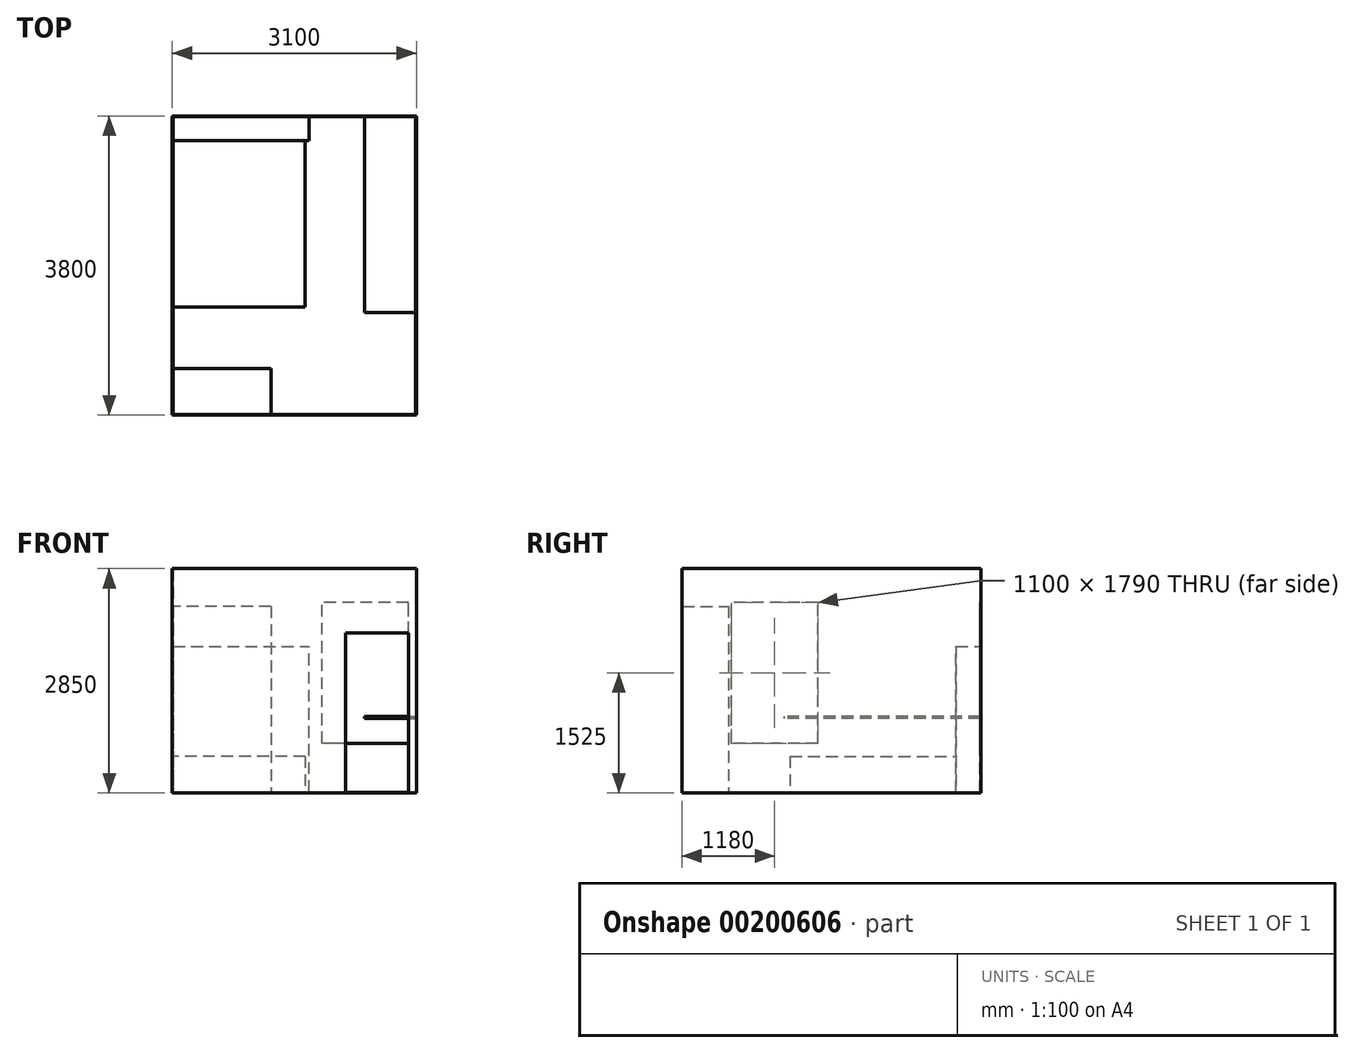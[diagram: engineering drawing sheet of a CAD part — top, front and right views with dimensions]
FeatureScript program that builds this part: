
annotation { "Feature Type Name" : "Feature", "Feature Type Description" : "" }
export const myFeature = defineFeature(function(context is Context, id is Id, definition is map)
    precondition{}
    {
        {
            var Q0;
            Q0=qCreatedBy(makeId("Top.planeOp"),FACE);
            var sketch = newSketch(context, id + "F0", { "sketchPlane" : qUnion([Q0])});
            skLineSegment(sketch, "E0.bottom", {"start": v(1550, -1900) * mm, "end": v(-1550, -1900) * mm});
            skLineSegment(sketch, "E0.top", {"start": v(1550, 1900) * mm, "end": v(-1550, 1900) * mm});
            skLineSegment(sketch, "E0.left", {"start": v(1550, -1900) * mm, "end": v(1550, 1900) * mm});
            skLineSegment(sketch, "E0.right", {"start": v(-1550, -1900) * mm, "end": v(-1550, 1900) * mm});
            skPoint(sketch, "E0.middle", {"position": v(0, 0) * mm});
            skSolve(sketch);
        }
        {
            var Q0;
            Q0 = qSketchRegion(id + "F0", true);
            extrude(context, id + "F1", {"entities" : qUnion([Q0]), "depth" : 2850 * mm});
        }
        {
            var Q0;
            Q0=makeQuery(id+"F1.opExtrude","CAP_FACE",FACE,{"disambiguationData":[OSD([sQuery(id+"F0.wireOp",EDGE,"E0.bottom"),sQuery(id+"F0.wireOp",EDGE,"E0.top"),sQuery(id+"F0.wireOp",EDGE,"E0.left"),sQuery(id+"F0.wireOp",EDGE,"E0.right")])],"isStart":false});
            shell(context, id + "F2", {"entities" : qUnion([Q0]), "thickness" : 10 * mm});
        }
        {
            var Q0;
            Q0=makeQuery(id+"F1.opExtrude","SWEPT_FACE",FACE,{"disambiguationData":[OSD([sQuery(id+"F0.wireOp",EDGE,"E0.bottom")])]});
            var sketch = newSketch(context, id + "F3", { "sketchPlane" : qUnion([Q0])});
            skLineSegment(sketch, "E1.bottom", {"start": v(650, 0) * mm, "end": v(1450, 0) * mm});
            skLineSegment(sketch, "E1.top", {"start": v(650, 2030) * mm, "end": v(1450, 2030) * mm});
            skLineSegment(sketch, "E1.left", {"start": v(650, 0) * mm, "end": v(650, 2030) * mm});
            skLineSegment(sketch, "E1.right", {"start": v(1450, 0) * mm, "end": v(1450, 2030) * mm});
            skSolve(sketch);
        }
        {
            var Q0;
            Q0 = qSketchRegion(id + "F3", true);
            extrude(context, id + "F4", {"entities" : qUnion([Q0]), "operationType" : NewBodyOperationType.REMOVE, "oppositeDirection" : true, "depth" : 10 * mm});
        }
        {
            var Q0;
            Q0=makeQuery(id+"F1.opExtrude","SWEPT_FACE",FACE,{"disambiguationData":[OSD([sQuery(id+"F0.wireOp",EDGE,"E0.right")])]});
            var sketch = newSketch(context, id + "F5", { "sketchPlane" : qUnion([Q0])});
            skLineSegment(sketch, "E2.bottom", {"start": v(170, 630) * mm, "end": v(1270, 630) * mm});
            skLineSegment(sketch, "E2.top", {"start": v(170, 2420) * mm, "end": v(1270, 2420) * mm});
            skLineSegment(sketch, "E2.left", {"start": v(170, 630) * mm, "end": v(170, 2420) * mm});
            skLineSegment(sketch, "E2.right", {"start": v(1270, 630) * mm, "end": v(1270, 2420) * mm});
            skSolve(sketch);
        }
        {
            var Q0;
            Q0 = qSketchRegion(id + "F5", true);
            extrude(context, id + "F6", {"entities" : qUnion([Q0]), "operationType" : NewBodyOperationType.REMOVE, "oppositeDirection" : true, "depth" : 10 * mm});
        }
        {
            var Q0;
            Q0=makeQuery(id+"F1.opExtrude","SWEPT_FACE",FACE,{"disambiguationData":[OSD([sQuery(id+"F0.wireOp",EDGE,"E0.top")])]});
            var sketch = newSketch(context, id + "F7", { "sketchPlane" : qUnion([Q0])});
            skLineSegment(sketch, "E3.bottom", {"start": v(-1450, 630) * mm, "end": v(-350, 630) * mm});
            skLineSegment(sketch, "E3.top", {"start": v(-1450, 2420) * mm, "end": v(-350, 2420) * mm});
            skLineSegment(sketch, "E3.left", {"start": v(-1450, 630) * mm, "end": v(-1450, 2420) * mm});
            skLineSegment(sketch, "E3.right", {"start": v(-350, 630) * mm, "end": v(-350, 2420) * mm});
            skSolve(sketch);
        }
        {
            var Q0;
            Q0 = qSketchRegion(id + "F7", true);
            extrude(context, id + "F8", {"entities" : qUnion([Q0]), "operationType" : NewBodyOperationType.REMOVE, "oppositeDirection" : true, "depth" : 10 * mm});
        }
        {
            var Q0;
            Q0=makeQuery(id+"F2.opShell","OFFSET_FACE",FACE,{"disambiguationData":[OSD([sQuery(id+"F0.wireOp",EDGE,"E0.bottom"),sQuery(id+"F0.wireOp",EDGE,"E0.top"),sQuery(id+"F0.wireOp",EDGE,"E0.left"),sQuery(id+"F0.wireOp",EDGE,"E0.right")])]});
            var sketch = newSketch(context, id + "F9", { "sketchPlane" : qUnion([Q0])});
            skLineSegment(sketch, "E4.bottom", {"start": v(-1540, -1890) * mm, "end": v(-295.4, -1890) * mm});
            skLineSegment(sketch, "E4.top", {"start": v(-1540, -1305.8) * mm, "end": v(-295.4, -1305.8) * mm});
            skLineSegment(sketch, "E4.left", {"start": v(-1540, -1890) * mm, "end": v(-1540, -1305.8) * mm});
            skLineSegment(sketch, "E4.right", {"start": v(-295.4, -1890) * mm, "end": v(-295.4, -1305.8) * mm});
            skSolve(sketch);
        }
        {
            var Q0;
            Q0 = qSketchRegion(id + "F9", true);
            var Q1;
            Q1 = qConstructionFilter(qBodyType(qCreatedBy(id + "F9" ,EDGE), BodyType.WIRE), ConstructionObject.NO);
            extrude(context, id + "F10", {"entities" : qUnion([Q0]), "operationType" : NewBodyOperationType.ADD, "surfaceEntities" : qUnion([Q1]), "depth" : 2362.2 * mm});
        }
        {
            var Q0;
            Q0=makeQuery(id+"F2.opShell","OFFSET_FACE",FACE,{"disambiguationData":[OSD([sQuery(id+"F0.wireOp",EDGE,"E0.top")])]});
            var sketch = newSketch(context, id + "F11", { "sketchPlane" : qUnion([Q0])});
            skLineSegment(sketch, "E5.bottom", {"start": v(-1540, 10) * mm, "end": v(187.2, 10) * mm});
            skLineSegment(sketch, "E5.top", {"start": v(-1540, 1864.2) * mm, "end": v(187.2, 1864.2) * mm});
            skLineSegment(sketch, "E5.left", {"start": v(-1540, 10) * mm, "end": v(-1540, 1864.2) * mm});
            skLineSegment(sketch, "E5.right", {"start": v(187.2, 10) * mm, "end": v(187.2, 1864.2) * mm});
            skSolve(sketch);
        }
        {
            var Q0;
            Q0 = qSketchRegion(id + "F11", true);
            extrude(context, id + "F12", {"entities" : qUnion([Q0]), "operationType" : NewBodyOperationType.ADD, "depth" : 304.8 * mm});
        }
        {
            var Q0;
            Q0=makeQuery(id+"F2.opShell","OFFSET_FACE",FACE,{"disambiguationData":[OSD([sQuery(id+"F0.wireOp",EDGE,"E0.left")])]});
            var sketch = newSketch(context, id + "F13", { "sketchPlane" : qUnion([Q0])});
            skLineSegment(sketch, "E6.bottom", {"start": v(-1890, 975.2) * mm, "end": v(599.2, 975.2) * mm});
            skLineSegment(sketch, "E6.top", {"start": v(-1890, 946.62) * mm, "end": v(599.2, 946.62) * mm});
            skLineSegment(sketch, "E6.left", {"start": v(-1890, 975.2) * mm, "end": v(-1890, 946.62) * mm});
            skLineSegment(sketch, "E6.right", {"start": v(599.2, 975.2) * mm, "end": v(599.2, 946.62) * mm});
            skSolve(sketch);
        }
        {
            var Q0;
            Q0 = qSketchRegion(id + "F13", true);
            extrude(context, id + "F14", {"entities" : qUnion([Q0]), "operationType" : NewBodyOperationType.ADD, "depth" : 650.88 * mm});
        }
        {
            var Q0;
            Q0=makeQuery(id+"F2.opShell","OFFSET_FACE",FACE,{"disambiguationData":[OSD([sQuery(id+"F0.wireOp",EDGE,"E0.bottom"),sQuery(id+"F0.wireOp",EDGE,"E0.top"),sQuery(id+"F0.wireOp",EDGE,"E0.left"),sQuery(id+"F0.wireOp",EDGE,"E0.right")])]});
            var sketch = newSketch(context, id + "F15", { "sketchPlane" : qUnion([Q0])});
            skLineSegment(sketch, "E7.bottom", {"start": v(-1540, 1585.2) * mm, "end": v(139.57, 1585.2) * mm});
            skLineSegment(sketch, "E7.top", {"start": v(-1540, -526.18) * mm, "end": v(139.58, -526.18) * mm});
            skLineSegment(sketch, "E7.left", {"start": v(-1540, 1585.2) * mm, "end": v(-1540, -526.17) * mm});
            skLineSegment(sketch, "E7.right", {"start": v(139.58, 1585.2) * mm, "end": v(139.58, -526.17) * mm});
            skSolve(sketch);
        }
        {
            var Q0;
            Q0 = qSketchRegion(id + "F15", true);
            extrude(context, id + "F16", {"entities" : qUnion([Q0]), "operationType" : NewBodyOperationType.ADD, "depth" : 457.2 * mm});
        }
    });
